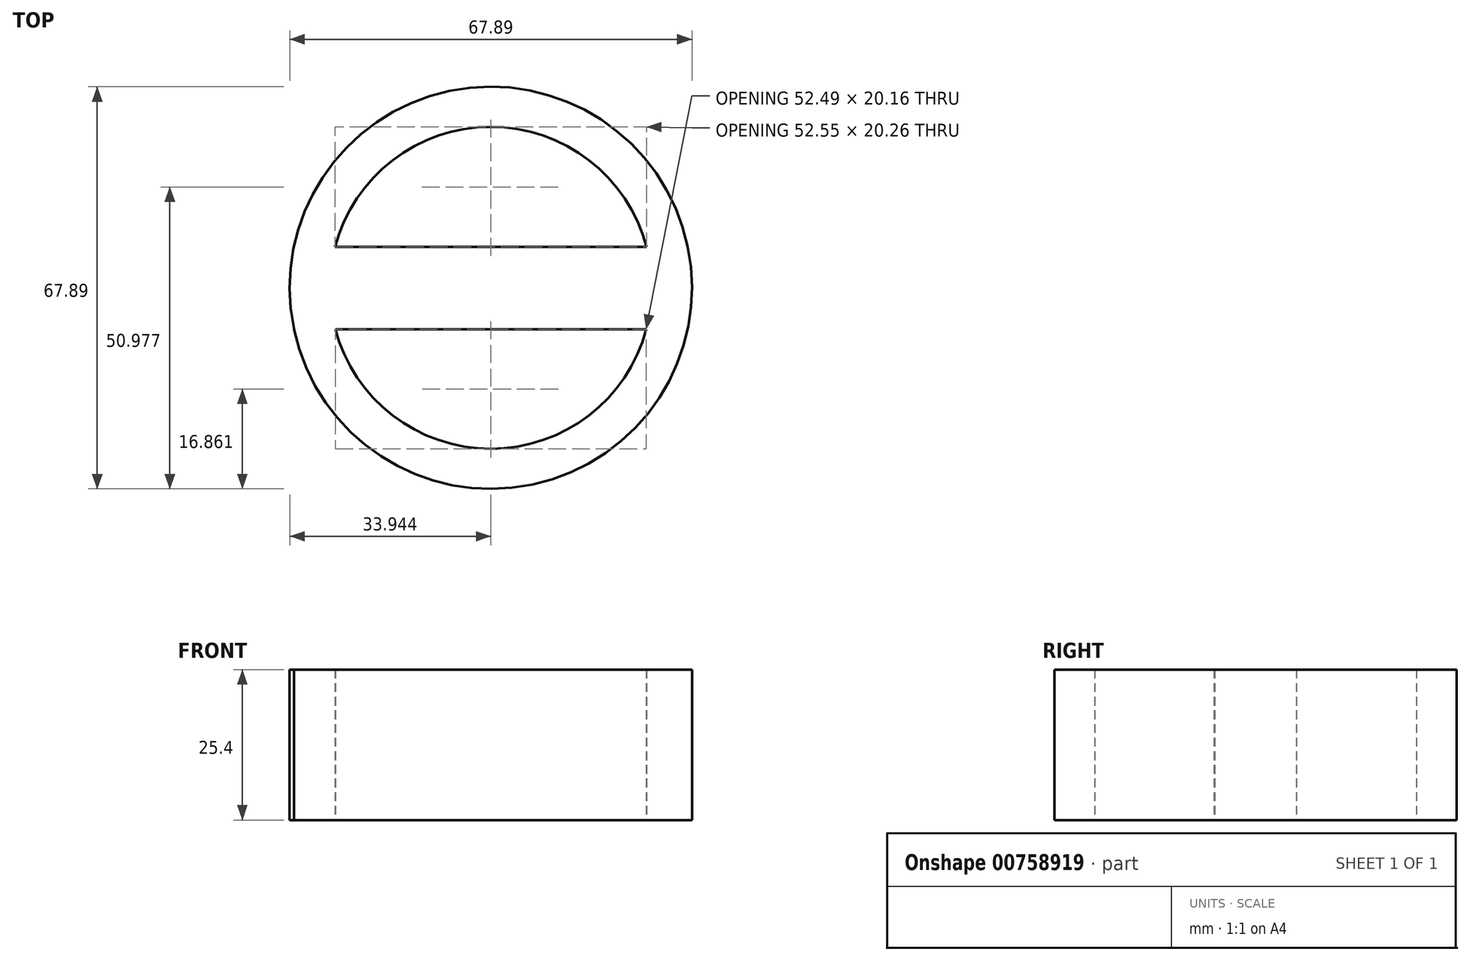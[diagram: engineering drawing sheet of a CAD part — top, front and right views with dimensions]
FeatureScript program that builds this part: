
annotation { "Feature Type Name" : "Feature", "Feature Type Description" : "" }
export const myFeature = defineFeature(function(context is Context, id is Id, definition is map)
    precondition{}
    {
        {
            var Q0;
            Q0=qCreatedBy(makeId("Top.planeOp"),FACE);
            var sketch = newSketch(context, id + "F0", { "sketchPlane" : qUnion([Q0])});
            skCircle(sketch, "E0", {"center": v(-5.09, -2.37) * mm, "radius": 12.33 * mm});
            skCircle(sketch, "E1", {"center": v(-5.09, -2.37) * mm, "radius": 19.4 * mm});
            skCircle(sketch, "E2", {"center": v(-5.09, -2.37) * mm, "radius": 33.95 * mm});
            skPoint(sketch, "E3.end.orphan", {"position": v(20.2, 0) * mm});
            skPoint(sketch, "E3.start.orphan", {"position": v(-30.38, 0) * mm});
            skCircle(sketch, "E4", {"center": v(-5.09, -2.37) * mm, "radius": 27.16 * mm});
            skLineSegment(sketch, "E5.bottom", {"start": v(-38.32, 4.54) * mm, "end": v(28.13, 4.54) * mm});
            skLineSegment(sketch, "E5.top", {"start": v(-38.32, -9.37) * mm, "end": v(28.13, -9.37) * mm});
            skLineSegment(sketch, "E5.left", {"start": v(-38.32, 4.54) * mm, "end": v(-38.32, -9.37) * mm});
            skLineSegment(sketch, "E5.right", {"start": v(28.13, 4.54) * mm, "end": v(28.13, -9.37) * mm});
            skSolve(sketch);
        }
        {
            var Q0;
            {var subQ0=sQuery(id+"F0.wireOp",EDGE,"E5.left");var subQ1=sQuery(id+"F0.wireOp",EDGE,"E2");var subQ3=makeQuery(id+"F0.imprint","INTERSECT",VERTEX,{"derivedFrom":[subQ1,subQ0]});Q0=makeQuery(id+"F0.imprint","IMPRINT",FACE,{"disambiguationData":[TD([[makeQuery(id+"F0.imprint","IMPRINT",EDGE,{"disambiguationData":[TD([[subQ3,1.0]])],"derivedFrom":subQ1}),1.0]])]});}
            var Q1;
            {var subQ0=sQuery(id+"F0.wireOp",EDGE,"E5.left");var subQ1=sQuery(id+"F0.wireOp",EDGE,"E2");var subQ2=makeQuery(id+"F0.imprint","INTERSECT",VERTEX,{"derivedFrom":[subQ1,subQ0]});Q1=makeQuery(id+"F0.imprint","IMPRINT",FACE,{"disambiguationData":[TD([[makeQuery(id+"F0.imprint","IMPRINT",EDGE,{"disambiguationData":[TD([[subQ2,-1.0]])],"derivedFrom":subQ1}),-1.0]])]});}
            var Q2;
            {var subQ0=sQuery(id+"F0.wireOp",EDGE,"E5.top");var subQ4=sQuery(id+"F0.wireOp",EDGE,"E4");var subQ6=makeQuery(id+"F0.imprint","INTERSECT",VERTEX,{"disambiguationData":[OD(0.0)],"derivedFrom":[subQ4,subQ0]});Q2=makeQuery(id+"F0.imprint","IMPRINT",FACE,{"disambiguationData":[TD([[makeQuery(id+"F0.imprint","IMPRINT",EDGE,{"disambiguationData":[TD([[subQ6,-1.0]])],"derivedFrom":subQ4}),-1.0]])]});}
            var Q3;
            {var subQ0=sQuery(id+"F0.wireOp",EDGE,"E5.right");Q3=makeQuery(id+"F0.imprint","IMPRINT",FACE,{"disambiguationData":[TD([[makeQuery(id+"F0.imprint","IMPRINT",EDGE,{"derivedFrom":subQ0}),1.0]])]});}
            var Q4;
            {var subQ0=sQuery(id+"F0.wireOp",EDGE,"E5.left");var subQ2=sQuery(id+"F0.wireOp",EDGE,"E2");var subQ9=makeQuery(id+"F0.imprint","INTERSECT",VERTEX,{"derivedFrom":[subQ2,subQ0]});Q4=makeQuery(id+"F0.imprint","IMPRINT",FACE,{"disambiguationData":[TD([[makeQuery(id+"F0.imprint","IMPRINT",EDGE,{"disambiguationData":[TD([[subQ9,-1.0]])],"derivedFrom":subQ2}),1.0]])]});}
            var Q5;
            {var subQ0=sQuery(id+"F0.wireOp",EDGE,"E5.bottom");var subQ1=sQuery(id+"F0.wireOp",EDGE,"E0");var subQ2=makeQuery(id+"F0.imprint","INTERSECT",VERTEX,{"disambiguationData":[OD(0.0)],"derivedFrom":[subQ1,subQ0]});Q5=makeQuery(id+"F0.imprint","IMPRINT",FACE,{"disambiguationData":[TD([[makeQuery(id+"F0.imprint","IMPRINT",EDGE,{"disambiguationData":[TD([[subQ2,-1.0]])],"derivedFrom":subQ1}),-1.0]])]});}
            var Q6;
            {var subQ0=sQuery(id+"F0.wireOp",EDGE,"E5.bottom");var subQ1=sQuery(id+"F0.wireOp",EDGE,"E0");var subQ2=makeQuery(id+"F0.imprint","INTERSECT",VERTEX,{"disambiguationData":[OD(1.0)],"derivedFrom":[subQ1,subQ0]});Q6=makeQuery(id+"F0.imprint","IMPRINT",FACE,{"disambiguationData":[TD([[makeQuery(id+"F0.imprint","IMPRINT",EDGE,{"disambiguationData":[TD([[subQ2,1.0]])],"derivedFrom":subQ1}),-1.0]])]});}
            var Q7;
            {var subQ0=sQuery(id+"F0.wireOp",EDGE,"E5.bottom");var subQ1=sQuery(id+"F0.wireOp",EDGE,"E0");var subQ2=makeQuery(id+"F0.imprint","INTERSECT",VERTEX,{"disambiguationData":[OD(0.0)],"derivedFrom":[subQ1,subQ0]});Q7=makeQuery(id+"F0.imprint","IMPRINT",FACE,{"disambiguationData":[TD([[makeQuery(id+"F0.imprint","IMPRINT",EDGE,{"disambiguationData":[TD([[subQ2,-1.0]])],"derivedFrom":subQ1}),1.0]])]});}
            var Q8;
            {var subQ0=sQuery(id+"F0.wireOp",EDGE,"E5.bottom");var subQ1=sQuery(id+"F0.wireOp",EDGE,"E1");var subQ2=makeQuery(id+"F0.imprint","INTERSECT",VERTEX,{"disambiguationData":[OD(0.0)],"derivedFrom":[subQ1,subQ0]});Q8=makeQuery(id+"F0.imprint","IMPRINT",FACE,{"disambiguationData":[TD([[makeQuery(id+"F0.imprint","IMPRINT",EDGE,{"disambiguationData":[TD([[subQ2,-1.0]])],"derivedFrom":subQ1}),-1.0]])]});}
            var Q9;
            {var subQ0=sQuery(id+"F0.wireOp",EDGE,"E5.bottom");var subQ1=sQuery(id+"F0.wireOp",EDGE,"E1");var subQ2=makeQuery(id+"F0.imprint","INTERSECT",VERTEX,{"disambiguationData":[OD(1.0)],"derivedFrom":[subQ1,subQ0]});Q9=makeQuery(id+"F0.imprint","IMPRINT",FACE,{"disambiguationData":[TD([[makeQuery(id+"F0.imprint","IMPRINT",EDGE,{"disambiguationData":[TD([[subQ2,1.0]])],"derivedFrom":subQ1}),-1.0]])]});}
            var Q10;
            {var subQ5=sQuery(id+"F0.wireOp",EDGE,"E5.right");Q10=makeQuery(id+"F0.imprint","IMPRINT",FACE,{"disambiguationData":[TD([[makeQuery(id+"F0.imprint","IMPRINT",EDGE,{"derivedFrom":subQ5}),-1.0]])]});}
            extrude(context, id + "F1", {"entities" : qUnion([Q0, Q1, Q2, Q3, Q4, Q5, Q6, Q7, Q8, Q9, Q10]), "depth" : 25.4 * mm, "offsetDistance" : 25.4 * mm});
        }
    });
